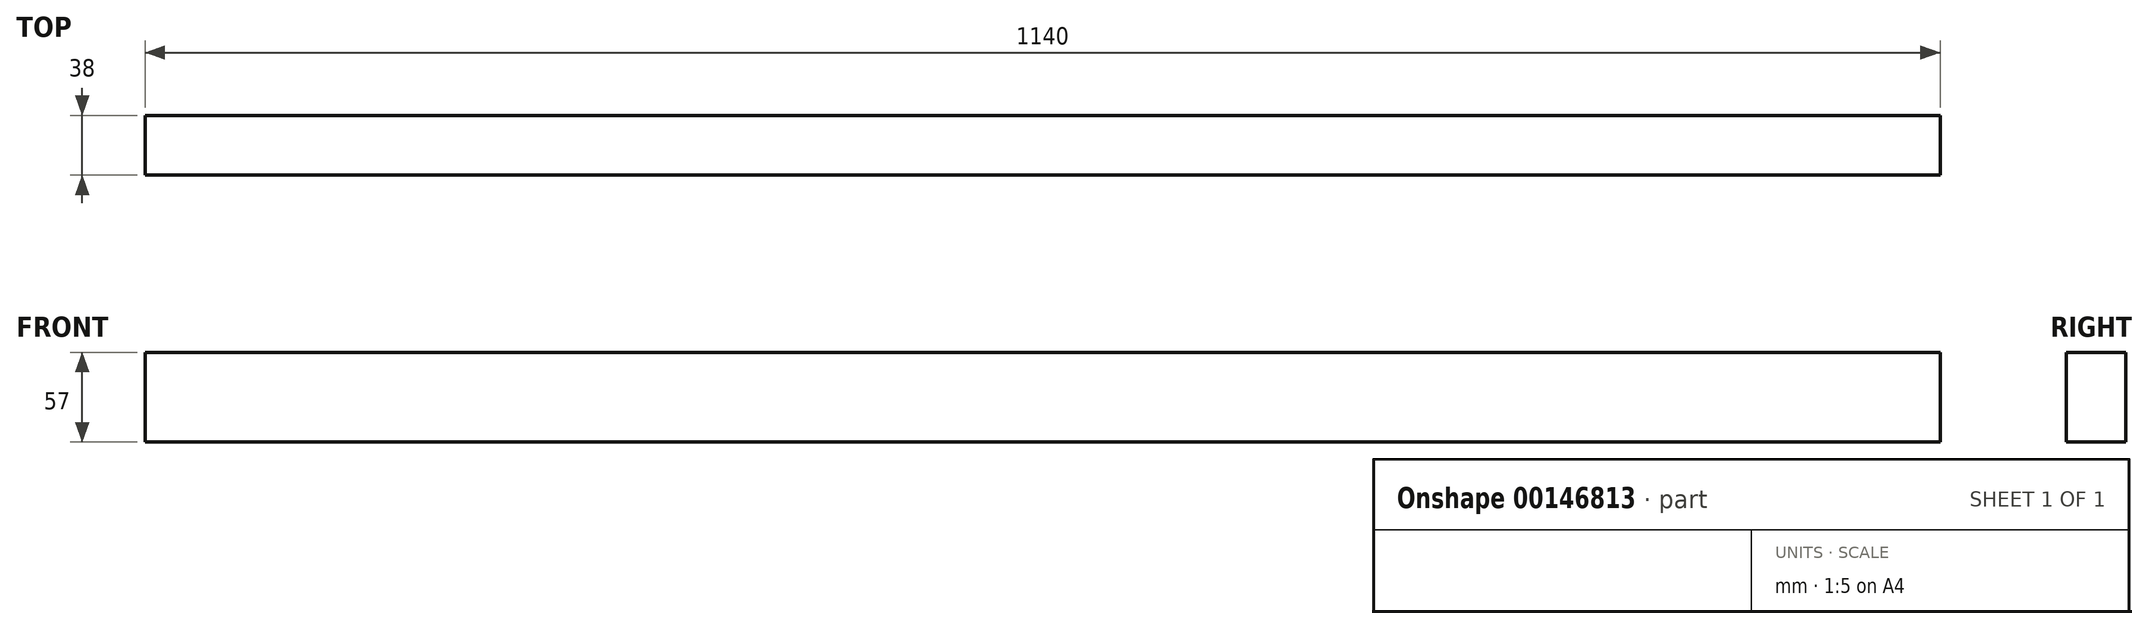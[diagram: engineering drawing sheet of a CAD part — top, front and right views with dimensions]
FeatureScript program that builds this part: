
annotation { "Feature Type Name" : "Feature", "Feature Type Description" : "" }
export const myFeature = defineFeature(function(context is Context, id is Id, definition is map)
    precondition{}
    {
        {
            var Q0;
            Q0=qCreatedBy(makeId("Top.planeOp"),FACE);
            var sketch = newSketch(context, id + "F0", { "sketchPlane" : qUnion([Q0])});
            skLineSegment(sketch, "E0.bottom", {"start": v(0, 0) * mm, "end": v(1140, 0) * mm});
            skLineSegment(sketch, "E0.top", {"start": v(0, 38) * mm, "end": v(1140, 38) * mm});
            skLineSegment(sketch, "E0.left", {"start": v(0, 0) * mm, "end": v(0, 38) * mm});
            skLineSegment(sketch, "E0.right", {"start": v(1140, 0) * mm, "end": v(1140, 38) * mm});
            skSolve(sketch);
        }
        {
            var Q0;
            Q0 = qSketchRegion(id + "F0", true);
            extrude(context, id + "F1", {"entities" : qUnion([Q0]), "depth" : 57 * mm});
        }
    });
